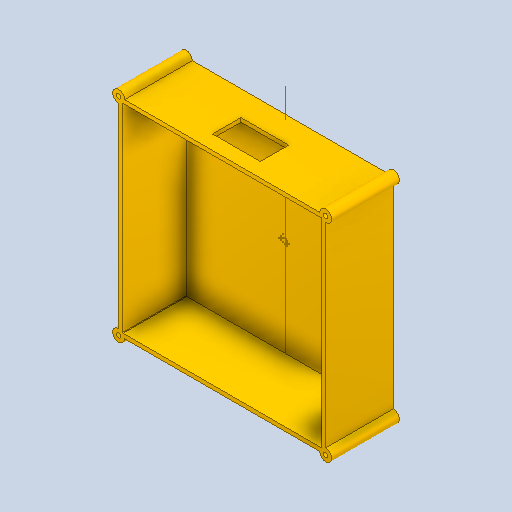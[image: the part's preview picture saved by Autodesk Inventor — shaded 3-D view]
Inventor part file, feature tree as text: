
AUTODESK INVENTOR PART (.ipt)
format: ipt  version: 2022 (Build 260153000, 153)  size: 183,808 bytes
history: native  units: in
note: dims shown in document units (in); Inventor stores cm internally (conversion verified against a paired STEP export)
features: extrude x4, sketch x4, shell x1
ambient origin geometry x8: Origin, YZ Plane, XZ Plane, XY Plane, X Axis, Y Axis, Z Axis, Center Point
bodies: Solid1 (feature_tree)
feature tree (9):
  extrude  "Extrusion1"  Depth=2.0in TaperAngle=0.0deg
  shell  "Shell1"  Thickness=0.125in
  extrude  "Extrusion2"  Depth=2.0in TaperAngle=0.0deg
  extrude  "Extrusion3"  Depth=4.25in TaperAngle=0.0deg
  extrude  "Extrusion4"  Depth=0.89in
  sketch  "Sketch1"  dims[d0=6.25in d1=2.0in d2=0.0in d3=0.125in]
  sketch  "Sketch2"  dims[d4=0.376in d5=2.0in d6=0.125in d7=0.0in d8=0.0in]
  sketch  "Sketch3"  dims[d9=0.1417in d10=4.25in d11=0.0in]
  sketch  "Sketch4"  dims[d12=1.5in d13=0.89in d14=0.45in d15=1.0in d16=0.0in]
